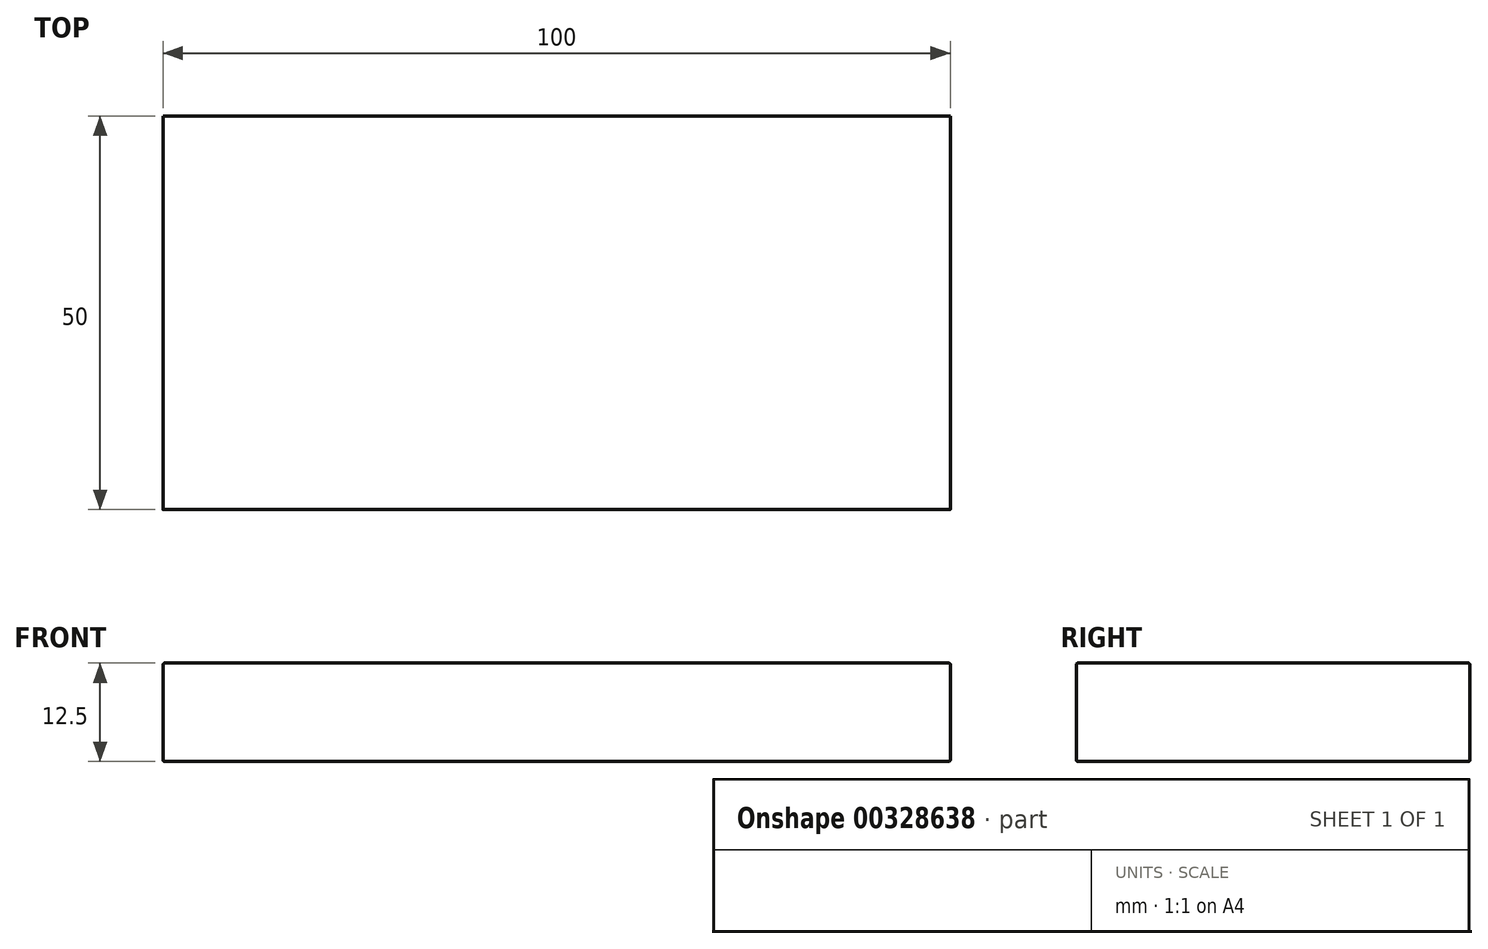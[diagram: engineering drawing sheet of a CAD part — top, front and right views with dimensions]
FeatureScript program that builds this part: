
annotation { "Feature Type Name" : "Feature", "Feature Type Description" : "" }
export const myFeature = defineFeature(function(context is Context, id is Id, definition is map)
    precondition{}
    {
        {
            var Q0;
            Q0=qCreatedBy(makeId("Top.planeOp"),FACE);
            var sketch = newSketch(context, id + "F0", { "sketchPlane" : qUnion([Q0])});
            skLineSegment(sketch, "E0.bottom", {"start": v(0, 0) * mm, "end": v(100, 0) * mm});
            skLineSegment(sketch, "E0.top", {"start": v(0, 50) * mm, "end": v(100, 50) * mm});
            skLineSegment(sketch, "E0.left", {"start": v(0, 0) * mm, "end": v(0, 50) * mm});
            skLineSegment(sketch, "E0.right", {"start": v(100, 0) * mm, "end": v(100, 50) * mm});
            skSolve(sketch);
        }
        {
            var Q0;
            Q0=qSketchRegion(id+"F0",true);
            extrude(context, id + "F1", {"entities" : qUnion([Q0]), "oppositeDirection" : true, "depth" : 12.5 * mm});
        }
        {
            var Q0;
            Q0=makeQuery(id+"F1.opExtrude","CAP_FACE",FACE,{"disambiguationData":[OSD([sQuery(id+"F0.wireOp",EDGE,"E0.bottom"),sQuery(id+"F0.wireOp",EDGE,"E0.top"),sQuery(id+"F0.wireOp",EDGE,"E0.left"),sQuery(id+"F0.wireOp",EDGE,"E0.right")])],"isStart":true});
            var Q1;
            Q1=makeQuery(id+"F1.opExtrude","CAP_FACE",FACE,{"disambiguationData":[OSD([sQuery(id+"F0.wireOp",EDGE,"E0.bottom"),sQuery(id+"F0.wireOp",EDGE,"E0.top"),sQuery(id+"F0.wireOp",EDGE,"E0.left"),sQuery(id+"F0.wireOp",EDGE,"E0.right")])],"isStart":false});
            fillet(context, id + "F2", {"entities" : qUnion([Q0, Q1]), "radius" : .2 * mm, "tangentPropagation" : true, "allowEdgeOverflow" : false});
        }
    });
